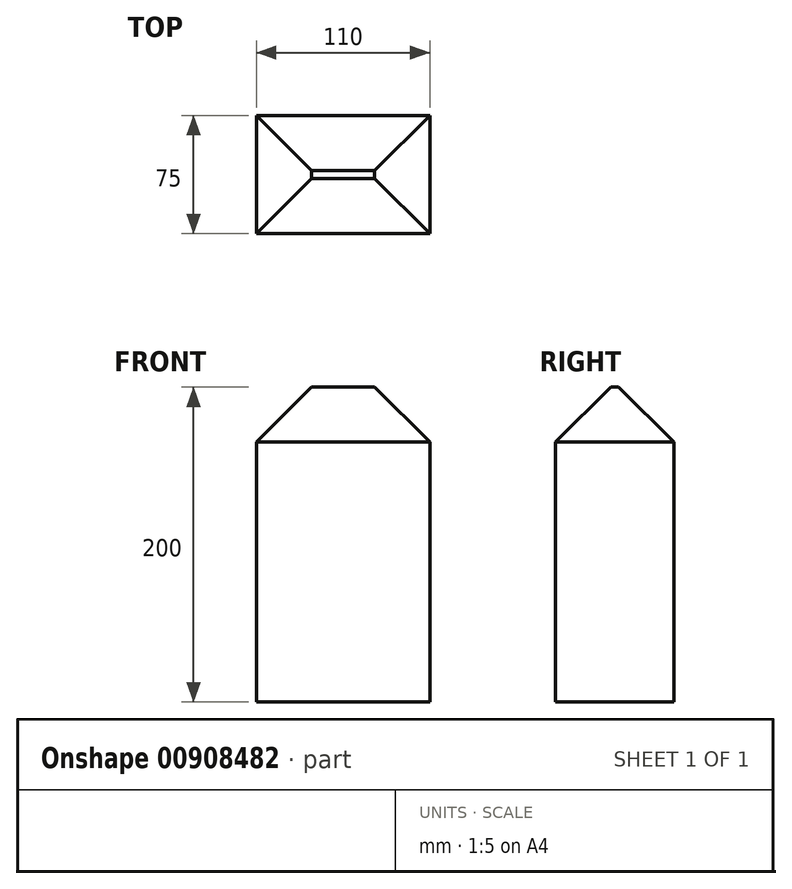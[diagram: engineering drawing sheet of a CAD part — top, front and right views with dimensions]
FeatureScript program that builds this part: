
annotation { "Feature Type Name" : "Feature", "Feature Type Description" : "" }
export const myFeature = defineFeature(function(context is Context, id is Id, definition is map)
    precondition{}
    {
        {
            var Q0;
            Q0=qCreatedBy(makeId("Top.planeOp"),FACE);
            var sketch = newSketch(context, id + "F0", { "sketchPlane" : qUnion([Q0])});
            skLineSegment(sketch, "E0.bottom", {"start": v(0, 0) * mm, "end": v(110, 0) * mm});
            skLineSegment(sketch, "E0.top", {"start": v(0, 75) * mm, "end": v(110, 75) * mm});
            skLineSegment(sketch, "E0.left", {"start": v(0, 0) * mm, "end": v(0, 75) * mm});
            skLineSegment(sketch, "E0.right", {"start": v(110, 0) * mm, "end": v(110, 75) * mm});
            skSolve(sketch);
        }
        {
            var Q0;
            Q0 = qSketchRegion(id + "F0", true);
            extrude(context, id + "F1", {"entities" : qUnion([Q0]), "depth" : 200 * mm, "offsetDistance" : 25 * mm});
        }
        {
            var Q0;
            Q0=makeQuery(id+"F1.opExtrude","CAP_EDGE",EDGE,{"disambiguationData":[OSD([sQuery(id+"F0.wireOp",EDGE,"E0.left")])],"isStart":false});
            var Q1;
            Q1=makeQuery(id+"F1.opExtrude","CAP_EDGE",EDGE,{"disambiguationData":[OSD([sQuery(id+"F0.wireOp",EDGE,"E0.bottom")])],"isStart":false});
            var Q2;
            Q2=makeQuery(id+"F1.opExtrude","CAP_FACE",FACE,{"disambiguationData":[OSD([sQuery(id+"F0.wireOp",EDGE,"E0.bottom"),sQuery(id+"F0.wireOp",EDGE,"E0.top"),sQuery(id+"F0.wireOp",EDGE,"E0.left"),sQuery(id+"F0.wireOp",EDGE,"E0.right")])],"isStart":false});
            chamfer(context, id + "F2", {"entities" : qUnion([Q0, Q1, Q2]), "width" : 35 * mm, "tangentPropagation" : true});
        }
    });
